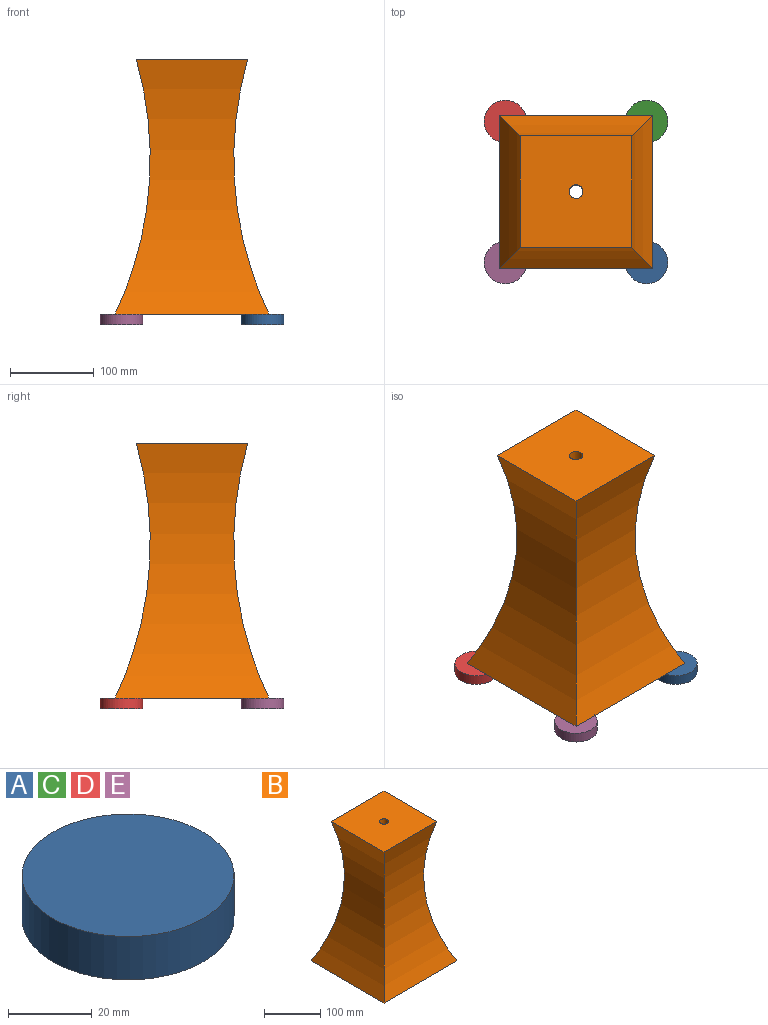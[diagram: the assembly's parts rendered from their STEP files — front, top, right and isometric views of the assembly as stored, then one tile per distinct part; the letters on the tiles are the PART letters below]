
ASSEMBLY  parts=5 mates=4
PART A: 3 faces, bbox 50.8x50.8x12.7 mm
  f0: cylinder r=25.4mm len=50.8mm, axis (0,0,-1), area 2026.8mm2, adj f1,f2
  f1: plane 50.8x50.8mm, normal (0,0,1), area 2026.8mm2, adj f0
  f2: plane 50.8x50.8mm, normal (0,0,-1), area 2026.8mm2, adj f0
PART B: 7 faces, bbox 184.2x184.2x304.8 mm
  f0: cylinder r=431.8mm len=304.8mm, axis (0,-1,0), area 38030.7mm2, adj f2,f3,f4,f5
  f1: cylinder r=431.8mm len=304.8mm, axis (0,-1,0), area 38030.7mm2, adj f2,f3,f4,f5
  f2: plane 184.15x184.15mm, normal (0,0,-1), area 33699.5mm2, adj f0,f1,f4,f5,f6
  f3: plane 133.35x133.35mm, normal (0,0,1), area 17570.5mm2, adj f0,f1,f4,f5,f6
  f4: cylinder r=431.8mm len=304.8mm, axis (1,0,0), area 38030.7mm2, adj f0,f1,f2,f3
  f5: cylinder r=431.8mm len=304.8mm, axis (1,0,0), area 38030.7mm2, adj f0,f1,f2,f3
  f6: cylinder r=8.21mm len=304.8mm, axis (0,0,1), area 15721.9mm2, adj f2,f3
PART C: same geometry as A
PART D: same geometry as A
PART E: same geometry as A
PLACE A t=(84.46,-84.46,-12.7)mm
PLACE B at identity
PLACE C t=(84.45,84.46,-12.7)mm
PLACE D t=(-84.45,84.46,-12.7)mm
PLACE E t=(-84.45,-84.46,-12.7)mm
MATE fastened D.f0 <-> B.f2  axis (0,0,1) through (-84.45,84.46,0)mm
MATE fastened A.f0 <-> B.f2  axis (0,0,1) through (84.46,-84.46,0)mm
MATE fastened E.f0 <-> B.f2  axis (0,0,1) through (-84.45,-84.46,0)mm
MATE fastened C.f0 <-> B.f2  axis (0,0,1) through (84.45,84.46,0)mm
